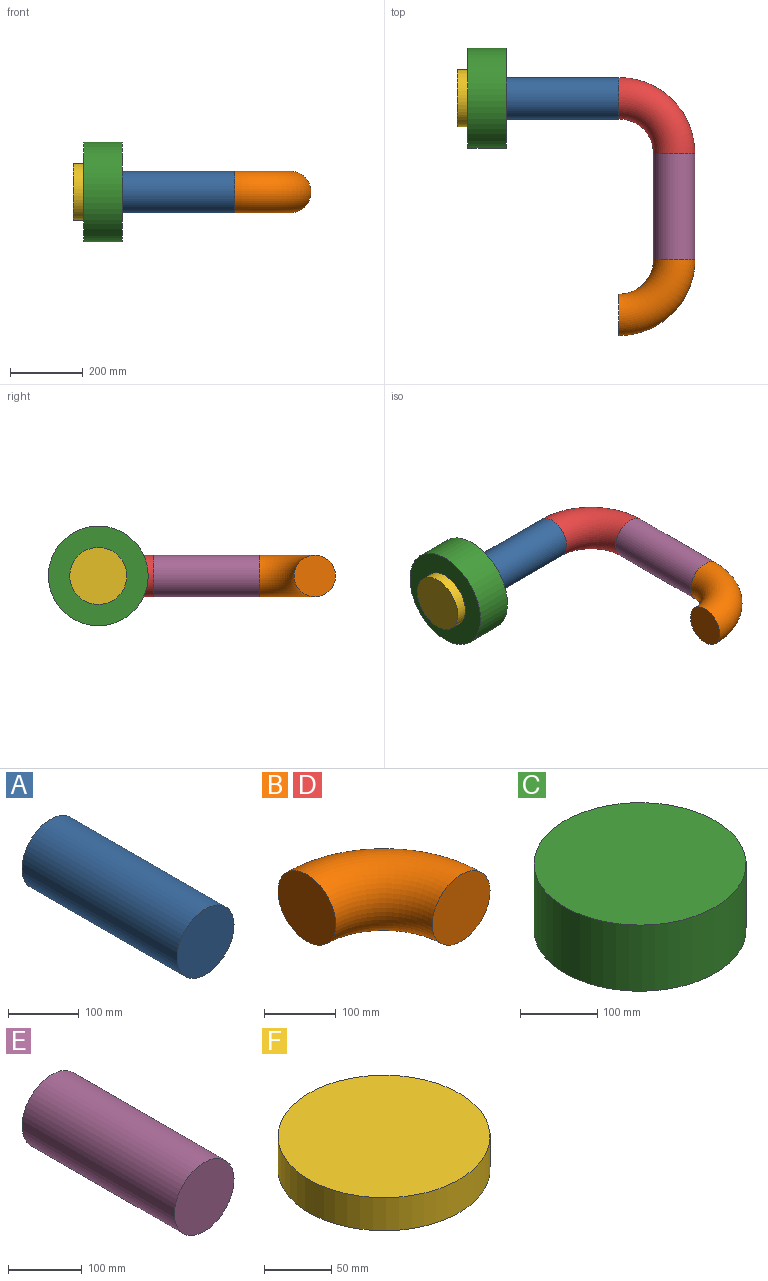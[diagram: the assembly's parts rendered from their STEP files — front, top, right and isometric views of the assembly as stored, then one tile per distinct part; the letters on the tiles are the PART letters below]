
ASSEMBLY  parts=6 mates=5
PART A: 3 faces, bbox 114.3x311x114.3 mm
  f0: cylinder r=57.15mm len=311mm, axis (0,1,0), area 111675.1mm2, adj f1,f2
  f1: plane 114.3x114.3mm, normal (0,-1,0), area 10260.8mm2, adj f0
  f2: plane 114.3x114.3mm, normal (0,1,0), area 10260.8mm2, adj f0
PART B: 3 faces, bbox 226.8x226.8x114.3 mm
  f0: plane 114.3x114.3mm, normal (0,-1,0), area 10260.8mm2, adj f2
  f1: plane 114.3x114.3mm, normal (-1,0,0), area 10260.8mm2, adj f2
  f2: torus R=152.4mm, axis (0,0,1), area 85960.9mm2, adj f0,f1
PART C: 3 faces, bbox 275x275x105 mm
  f0: cylinder r=137.5mm len=275mm, axis (0,0,-1), area 90713.5mm2, adj f1,f2
  f1: plane 275x275mm, normal (0,0,1), area 59395.7mm2, adj f0
  f2: plane 275x275mm, normal (0,0,-1), area 59395.7mm2, adj f0
PART D: same geometry as B
PART E: 3 faces, bbox 114.3x292.2x114.3 mm
  f0: cylinder r=57.15mm len=292.2mm, axis (0,1,0), area 104924.4mm2, adj f1,f2
  f1: plane 114.3x114.3mm, normal (0,-1,0), area 10260.8mm2, adj f0
  f2: plane 114.3x114.3mm, normal (0,1,0), area 10260.8mm2, adj f0
PART F: 3 faces, bbox 157.2x157.2x30 mm
  f0: cylinder r=78.6mm len=157.2mm, axis (0,0,-1), area 14815.8mm2, adj f1,f2
  f1: plane 157.2x157.2mm, normal (0,0,1), area 19408.6mm2, adj f0
  f2: plane 157.2x157.2mm, normal (0,0,-1), area 19408.6mm2, adj f0
PLACE A rot(axis=(0,0,1),90deg) t=(-310.22,603.84,0)mm
PLACE B rot(axis=(0,0,-1),90deg) t=(0.78,6.84,0)mm
PLACE C rot(axis=(0,1,0),90deg) t=(-415.22,603.84,0)mm
PLACE D t=(153.18,451.44,0)mm
PLACE E t=(153.18,451.44,0)mm
PLACE F rot(axis=(0,-1,0),90deg) t=(-415.22,603.84,0)mm
MATE fastened D.f0 <-> E.f0  axis (0,-1,0) through (153.18,451.44,0)mm
MATE fastened C.f0 <-> A.f0  axis (1,0,0) through (-310.22,603.84,0)mm
MATE fastened E.f0 <-> B.f1  axis (0,-1,0) through (153.18,159.24,0)mm
MATE fastened F.f0 <-> C.f0  axis (1,0,0) through (-415.22,603.84,0)mm
MATE fastened A.f0 <-> D.f1  axis (1,0,0) through (0.78,603.84,0)mm
